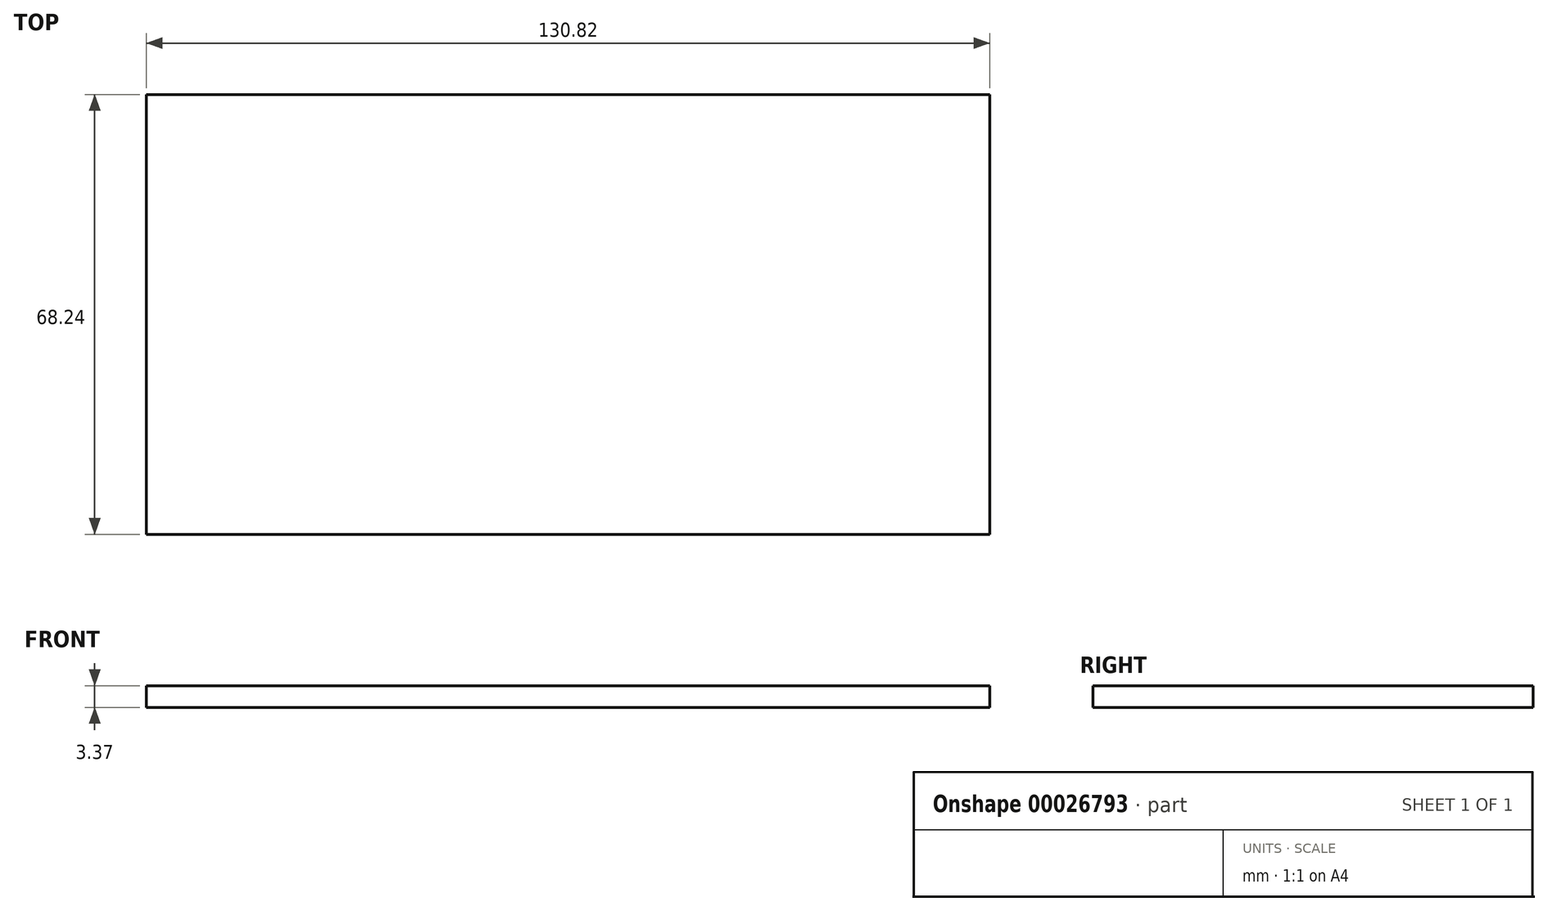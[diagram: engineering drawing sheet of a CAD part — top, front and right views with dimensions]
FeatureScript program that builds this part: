
annotation { "Feature Type Name" : "Feature", "Feature Type Description" : "" }
export const myFeature = defineFeature(function(context is Context, id is Id, definition is map)
    precondition{}
    {
        {
            var Q0;
            Q0=qCreatedBy(makeId("Top.planeOp"),FACE);
            var sketch = newSketch(context, id + "F0", { "sketchPlane" : qUnion([Q0])});
            skLineSegment(sketch, "E0.bottom", {"start": v(-65.56, 35.6) * mm, "end": v(65.26, 35.6) * mm});
            skLineSegment(sketch, "E0.top", {"start": v(-65.56, -32.63) * mm, "end": v(65.26, -32.63) * mm});
            skLineSegment(sketch, "E0.left", {"start": v(-65.56, 35.6) * mm, "end": v(-65.56, -32.63) * mm});
            skLineSegment(sketch, "E0.right", {"start": v(65.26, 35.6) * mm, "end": v(65.26, -32.63) * mm});
            skSolve(sketch);
        }
        {
            var Q0;
            Q0=makeQuery(id+"F0.imprint","IMPRINT",FACE,{"disambiguationData":[TD([[makeQuery(id+"F0.imprint","IMPRINT",EDGE,{"derivedFrom":sQuery(id+"F0.wireOp",EDGE,"E0.bottom")}),-1.0]])]});
            extrude(context, id + "F1", {"entities" : qUnion([Q0]), "depth" : 3.37 * mm});
        }
    });
